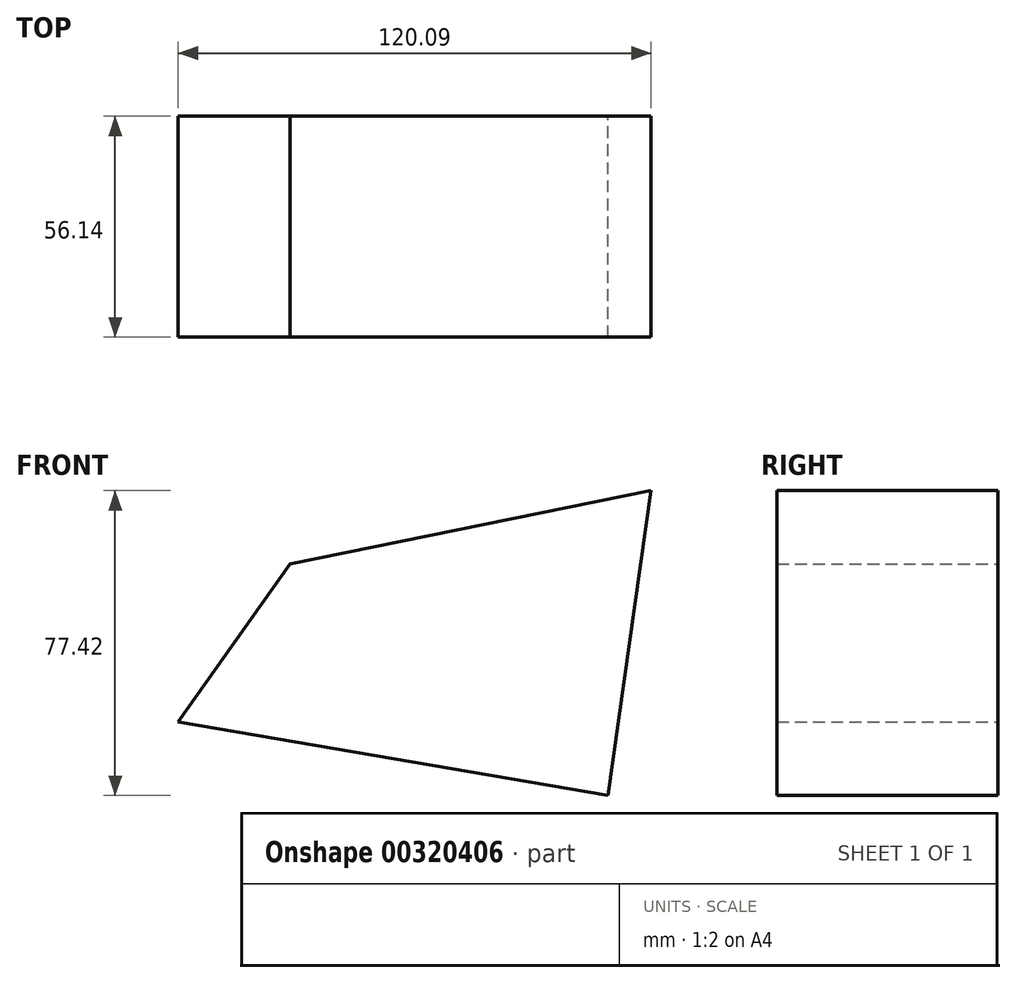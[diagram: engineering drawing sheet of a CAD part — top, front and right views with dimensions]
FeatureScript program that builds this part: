
annotation { "Feature Type Name" : "Feature", "Feature Type Description" : "" }
export const myFeature = defineFeature(function(context is Context, id is Id, definition is map)
    precondition{}
    {
        {
            var Q0;
            Q0=qCreatedBy(makeId("Front.planeOp"),FACE);
            var sketch = newSketch(context, id + "F0", { "sketchPlane" : qUnion([Q0])});
            skLineSegment(sketch, "E0", {"start": v(-35.05, 20.27) * mm, "end": v(-63.4, -19.96) * mm});
            skLineSegment(sketch, "E1", {"start": v(-63.4, -19.96) * mm, "end": v(45.72, -38.56) * mm});
            skLineSegment(sketch, "E2", {"start": v(45.72, -38.56) * mm, "end": v(56.7, 38.86) * mm});
            skLineSegment(sketch, "E3", {"start": v(56.7, 38.86) * mm, "end": v(-35.05, 20.27) * mm});
            skSolve(sketch);
        }
        {
            var Q0;
            Q0 = qSketchRegion(id + "F0", true);
            extrude(context, id + "F1", {"entities" : qUnion([Q0]), "endBound" : BoundingType.SYMMETRIC, "depth" : 56.13 * mm});
        }
    });
